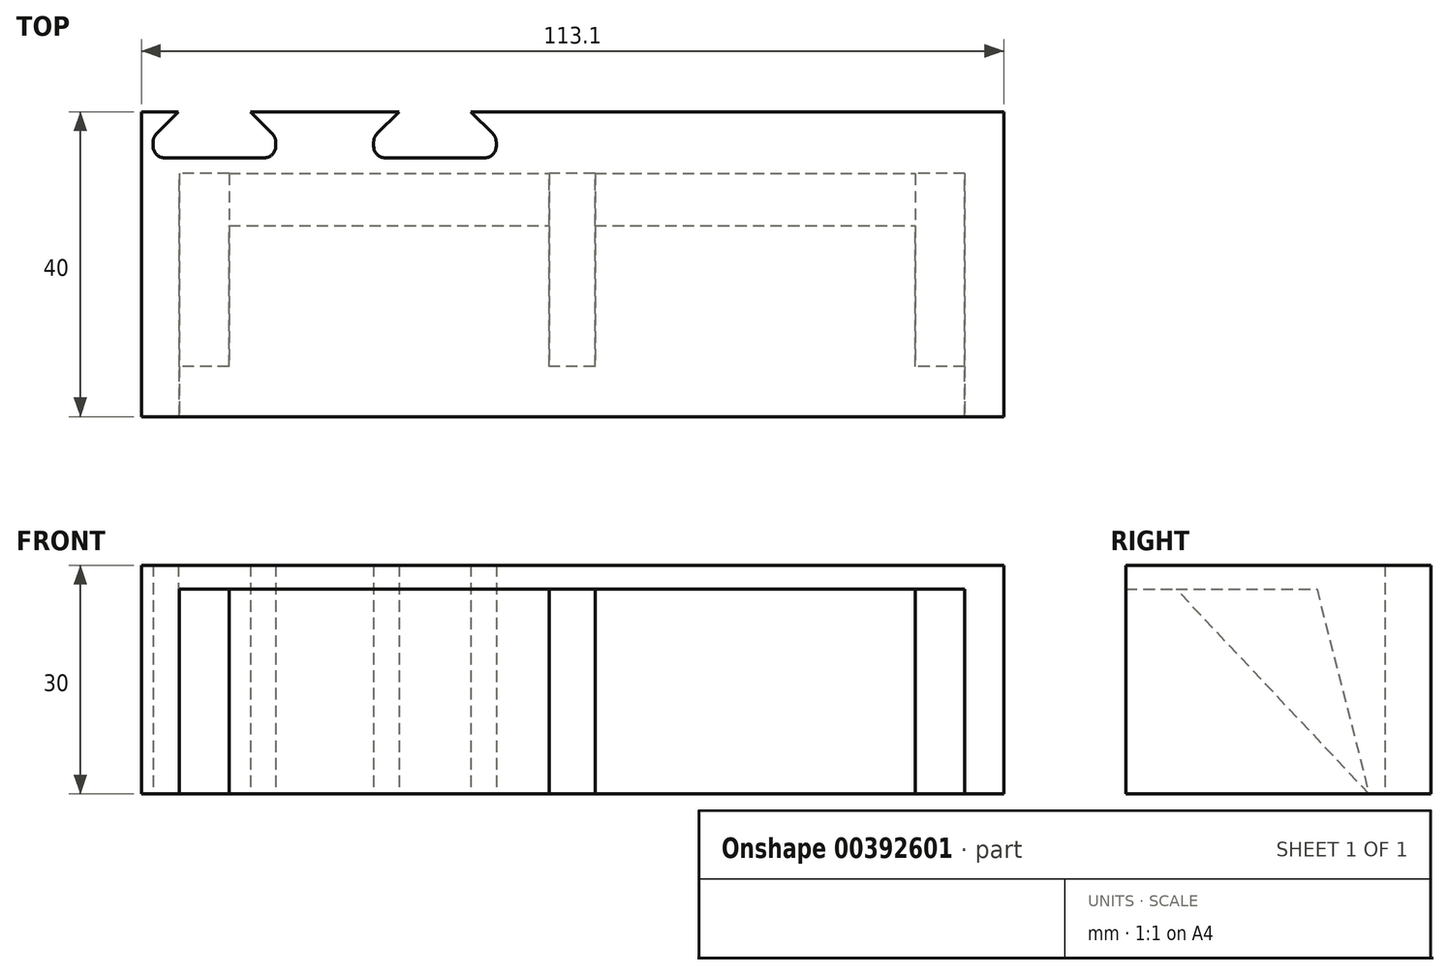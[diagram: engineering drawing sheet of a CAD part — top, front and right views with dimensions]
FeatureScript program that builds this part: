
annotation { "Feature Type Name" : "Feature", "Feature Type Description" : "" }
export const myFeature = defineFeature(function(context is Context, id is Id, definition is map)
    precondition{}
    {
        {
            var Q0;
            Q0=qCreatedBy(makeId("Top.planeOp"),FACE);
            var sketch = newSketch(context, id + "F0", { "sketchPlane" : qUnion([Q0])});
            skLineSegment(sketch, "E0.bottom", {"start": v(90, -35) * mm, "end": v(0, -35) * mm});
            skLineSegment(sketch, "E0.top", {"start": v(90, 35) * mm, "end": v(0, 35) * mm});
            skLineSegment(sketch, "E0.left", {"start": v(90, -35) * mm, "end": v(90, 35) * mm});
            skPoint(sketch, "E0.middle", {"position": v(0, 0) * mm});
            skPoint(sketch, "E1.middle", {"position": v(49.8, 0) * mm});
            skLineSegment(sketch, "E2", {"start": v(0, 0) * mm, "end": v(24, 0) * mm, "construction": true});
            skLineSegment(sketch, "E3", {"start": v(0, 0) * mm, "end": v(0, -14) * mm, "construction": true});
            skLineSegment(sketch, "E4", {"start": v(0, 0) * mm, "end": v(-35, 0) * mm, "construction": true});
            skLineSegment(sketch, "E5.bottom", {"start": v(-5, -19.5) * mm, "end": v(5, -19.5) * mm});
            skLineSegment(sketch, "E5.top", {"start": v(-5, 19.5) * mm, "end": v(5, 19.5) * mm});
            skLineSegment(sketch, "E5.left", {"start": v(-5, -19.5) * mm, "end": v(-5, 19.5) * mm});
            skLineSegment(sketch, "E5.right", {"start": v(5, -19.5) * mm, "end": v(5, 19.5) * mm});
            skLineSegment(sketch, "E6.bottom", {"start": v(-40, -17.25) * mm, "end": v(-30, -17.25) * mm});
            skLineSegment(sketch, "E6.top", {"start": v(-40, 17.25) * mm, "end": v(-30, 17.25) * mm});
            skLineSegment(sketch, "E6.left", {"start": v(-40, -17.25) * mm, "end": v(-40, 17.25) * mm});
            skLineSegment(sketch, "E6.right", {"start": v(-30, -17.25) * mm, "end": v(-30, 17.25) * mm});
            skPoint(sketch, "E6.middle", {"position": v(-35, 0) * mm});
            skLineSegment(sketch, "E7", {"start": v(0, 35) * mm, "end": v(0, 23) * mm});
            skPoint(sketch, "E7.endSnap0", {"position": v(0, 35) * mm});
            skLineSegment(sketch, "E8", {"start": v(0, 23) * mm, "end": v(-50, 23) * mm});
            skLineSegment(sketch, "E9", {"start": v(-50, 23) * mm, "end": v(-50, 0) * mm});
            skLineSegment(sketch, "E10.MirrorCS", {"start": v(-50, -23) * mm, "end": v(-50, 0) * mm});
            skLineSegment(sketch, "E11.MirrorCS", {"start": v(0, -35) * mm, "end": v(0, -23) * mm});
            skLineSegment(sketch, "E12.MirrorCS", {"start": v(0, -23) * mm, "end": v(-50, -23) * mm});
            skPoint(sketch, "E0.right.end.orphan", {"position": v(-90, 35) * mm});
            skPoint(sketch, "E13.orphan", {"position": v(-90, -35) * mm});
            skLineSegment(sketch, "E14.0", {"start": v(92.1, -37.1) * mm, "end": v(92.1, 37.1) * mm});
            skLineSegment(sketch, "E14.1", {"start": v(92.1, -37.1) * mm, "end": v(-2.1, -37.1) * mm});
            skLineSegment(sketch, "E14.2", {"start": v(92.1, 37.1) * mm, "end": v(-2.1, 37.1) * mm});
            skLineSegment(sketch, "E14.3", {"start": v(-2.1, -37.1) * mm, "end": v(-2.1, -25.1) * mm});
            skLineSegment(sketch, "E14.4", {"start": v(-2.1, -25.1) * mm, "end": v(-52.1, -25.1) * mm});
            skLineSegment(sketch, "E14.5", {"start": v(-2.1, 37.1) * mm, "end": v(-2.1, 25.1) * mm});
            skLineSegment(sketch, "E14.6", {"start": v(-2.1, 25.1) * mm, "end": v(-52.1, 25.1) * mm});
            skLineSegment(sketch, "E14.7", {"start": v(-52.1, 25.1) * mm, "end": v(-52.1, 0) * mm});
            skLineSegment(sketch, "E14.8", {"start": v(-52.1, -25.1) * mm, "end": v(-52.1, 0) * mm});
            skLineSegment(sketch, "E15.bottom", {"start": v(-30, 52.75) * mm, "end": v(-40, 52.75) * mm});
            skLineSegment(sketch, "E15.top", {"start": v(-30, 87.25) * mm, "end": v(-40, 87.25) * mm});
            skLineSegment(sketch, "E15.left", {"start": v(-30, 52.75) * mm, "end": v(-30, 87.25) * mm});
            skLineSegment(sketch, "E15.right", {"start": v(-40, 52.75) * mm, "end": v(-40, 87.25) * mm});
            skPoint(sketch, "E15.middle", {"position": v(-35, 70) * mm});
            skLineSegment(sketch, "E16.bottom", {"start": v(-5, 50.5) * mm, "end": v(5, 50.5) * mm});
            skLineSegment(sketch, "E16.top", {"start": v(-5, 89.5) * mm, "end": v(5, 89.5) * mm});
            skLineSegment(sketch, "E16.left", {"start": v(-5, 50.5) * mm, "end": v(-5, 89.5) * mm});
            skLineSegment(sketch, "E16.right", {"start": v(5, 50.5) * mm, "end": v(5, 89.5) * mm});
            skPoint(sketch, "E16.middle", {"position": v(0, 70) * mm});
            skPoint(sketch, "E16.middle.positionSnap0", {"position": v(-30, 70) * mm});
            skPoint(sketch, "E16.centerSnap0", {"position": v(-30, 70) * mm});
            skLineSegment(sketch, "E17", {"start": v(-35, 0) * mm, "end": v(-35, 70) * mm, "construction": true});
            skCircle(sketch, "E18", {"center": v(0, -14) * mm, "radius": 2 * mm});
            skLineSegment(sketch, "E19", {"start": v(-35, 0) * mm, "end": v(-35, -11.75) * mm, "construction": true});
            skCircle(sketch, "E20", {"center": v(-35, -11.75) * mm, "radius": 2 * mm});
            skCircle(sketch, "E21.MirrorC", {"center": v(-35, 11.75) * mm, "radius": 2 * mm});
            skCircle(sketch, "E22.MirrorC", {"center": v(0, 14) * mm, "radius": 2 * mm});
            skLineSegment(sketch, "E23", {"start": v(-35, 70) * mm, "end": v(-35, 81.75) * mm, "construction": true});
            skLineSegment(sketch, "E24", {"start": v(0, 70) * mm, "end": v(0, 84) * mm, "construction": true});
            skCircle(sketch, "E25", {"center": v(-35, 81.75) * mm, "radius": 2 * mm});
            skCircle(sketch, "E26", {"center": v(0, 84) * mm, "radius": 2 * mm});
            skLineSegment(sketch, "E27", {"start": v(-35, 70) * mm, "end": v(-30, 70) * mm, "construction": true});
            skCircle(sketch, "E28.MirrorC", {"center": v(-35, 58.25) * mm, "radius": 2 * mm});
            skCircle(sketch, "E29.MirrorC", {"center": v(0, 56) * mm, "radius": 2 * mm});
            skLineSegment(sketch, "E30", {"start": v(90, -35) * mm, "end": v(92.1, -35) * mm});
            skLineSegment(sketch, "E31", {"start": v(90, 35) * mm, "end": v(92.1, 35) * mm});
            skLineSegment(sketch, "E32", {"start": v(-2.1, 37.1) * mm, "end": v(-6.1, 37.1) * mm});
            skLineSegment(sketch, "E33", {"start": v(-6.1, 37.1) * mm, "end": v(-6.1, 25.1) * mm});
            skLineSegment(sketch, "E34", {"start": v(-2.1, -37.1) * mm, "end": v(-6.1, -37.1) * mm});
            skLineSegment(sketch, "E35", {"start": v(-6.1, -37.1) * mm, "end": v(-6.1, -25.1) * mm});
            skLineSegment(sketch, "E36", {"start": v(-41, 23) * mm, "end": v(-41, 11) * mm});
            skLineSegment(sketch, "E37", {"start": v(-41, 11) * mm, "end": v(-50, 11) * mm});
            skPoint(sketch, "E38.end.orphan", {"position": v(-41, 14.45) * mm});
            skLineSegment(sketch, "E39.MirrorCS", {"start": v(-41, -11) * mm, "end": v(-50, -11) * mm});
            skLineSegment(sketch, "E40.MirrorCS", {"start": v(-41, -23) * mm, "end": v(-41, -11) * mm});
            skLineSegment(sketch, "E41", {"start": v(90, -35) * mm, "end": v(90, -37.1) * mm});
            skLineSegment(sketch, "E42", {"start": v(90, 35) * mm, "end": v(90, 37.1) * mm});
            skLineSegment(sketch, "E43.bottom", {"start": v(90, 35) * mm, "end": v(86, 35) * mm});
            skLineSegment(sketch, "E43.left", {"start": v(90, 35) * mm, "end": v(90, 23) * mm});
            skLineSegment(sketch, "E44.bottom", {"start": v(90, -35) * mm, "end": v(86, -35) * mm});
            skLineSegment(sketch, "E44.left", {"start": v(90, -35) * mm, "end": v(90, -23) * mm});
            skLineSegment(sketch, "E45.bottom", {"start": v(86, -35) * mm, "end": v(80, -35) * mm});
            skLineSegment(sketch, "E46.bottom", {"start": v(86, 35) * mm, "end": v(80, 35) * mm});
            skLineSegment(sketch, "E47.bottom", {"start": v(0, 23) * mm, "end": v(7, 23) * mm});
            skLineSegment(sketch, "E47.top", {"start": v(0, 35) * mm, "end": v(12, 35) * mm});
            skLineSegment(sketch, "E47.left", {"start": v(0, 23) * mm, "end": v(0, 35) * mm});
            skLineSegment(sketch, "E47.right", {"start": v(12, 28) * mm, "end": v(12, 35) * mm});
            skLineSegment(sketch, "E48.bottom", {"start": v(0, -35) * mm, "end": v(12, -35) * mm});
            skLineSegment(sketch, "E48.top", {"start": v(0, -23) * mm, "end": v(7, -23) * mm});
            skLineSegment(sketch, "E48.right", {"start": v(12, -35) * mm, "end": v(12, -28) * mm});
            skCircle(sketch, "E49", {"center": v(6, -29) * mm, "radius": 2 * mm});
            skPoint(sketch, "E49.centerSnap0", {"position": v(6, -35) * mm});
            skPoint(sketch, "E49.centerSnap1", {"position": v(0, -29) * mm});
            skPoint(sketch, "E50.visualSharp", {"position": v(12, -23) * mm});
            skArc(sketch, "E50.filletArc", {"start": v(12, -28) * mm, "mid": v(10.54, -24.46) * mm, "end": v(7, -23) * mm});
            skPoint(sketch, "E51.visualSharp", {"position": v(12, 23) * mm});
            skArc(sketch, "E51.filletArc", {"start": v(7, 23) * mm, "mid": v(10.54, 24.46) * mm, "end": v(12, 28) * mm});
            skCircle(sketch, "E52.MirrorC", {"center": v(6, 29) * mm, "radius": 2 * mm});
            skCircle(sketch, "E53", {"center": v(6, 29) * mm, "radius": 4.5 * mm});
            skCircle(sketch, "E54.MirrorC", {"center": v(6, -29) * mm, "radius": 4.5 * mm});
            skCircle(sketch, "E55", {"center": v(0, 14) * mm, "radius": 6 * mm});
            skCircle(sketch, "E56", {"center": v(-35, 11.75) * mm, "radius": 6 * mm});
            skCircle(sketch, "E57", {"center": v(-35, -11.75) * mm, "radius": 6 * mm});
            skCircle(sketch, "E58", {"center": v(0, -14) * mm, "radius": 6 * mm});
            skLineSegment(sketch, "E59", {"start": v(-6.1, 25.1) * mm, "end": v(-6.08, 23) * mm});
            skLineSegment(sketch, "E60", {"start": v(-6.1, -25.1) * mm, "end": v(-6.1, -23) * mm});
            skLineSegment(sketch, "E61", {"start": v(-47.66, 23) * mm, "end": v(-47.66, 18) * mm, "construction": true});
            skLineSegment(sketch, "E62", {"start": v(-50, 18) * mm, "end": v(-45, 18) * mm, "construction": true});
            skCircle(sketch, "E63", {"center": v(-45, 18) * mm, "radius": 2.25 * mm});
            skCircle(sketch, "E64.MirrorC", {"center": v(-45, -18) * mm, "radius": 2.25 * mm});
            skCircle(sketch, "E65.MirrorC", {"center": v(-25, 18) * mm, "radius": 2.25 * mm});
            skCircle(sketch, "E66.MirrorC", {"center": v(-25, -18) * mm, "radius": 2.25 * mm});
            skCircle(sketch, "E67.MirrorC", {"center": v(28.54, -17.75) * mm, "radius": 2.25 * mm});
            skLineSegment(sketch, "E68.bottom", {"start": v(34.04, -22.75) * mm, "end": v(23.04, -22.75) * mm});
            skLineSegment(sketch, "E68.top", {"start": v(34.04, -12.75) * mm, "end": v(23.04, -12.75) * mm});
            skLineSegment(sketch, "E68.left", {"start": v(36.04, -20.75) * mm, "end": v(36.04, -14.75) * mm});
            skLineSegment(sketch, "E68.right", {"start": v(21.04, -20.75) * mm, "end": v(21.04, -14.75) * mm});
            skLineSegment(sketch, "E69.0", {"start": v(36.44, -12.35) * mm, "end": v(20.64, -12.35) * mm});
            skLineSegment(sketch, "E69.1", {"start": v(36.44, -23.15) * mm, "end": v(36.44, -12.35) * mm});
            skLineSegment(sketch, "E69.2", {"start": v(36.44, -23.15) * mm, "end": v(20.64, -23.15) * mm});
            skLineSegment(sketch, "E69.3", {"start": v(20.64, -23.15) * mm, "end": v(20.64, -12.35) * mm});
            skPoint(sketch, "E70.visualSharp", {"position": v(21.04, -12.75) * mm});
            skArc(sketch, "E70.filletArc", {"start": v(23.04, -12.75) * mm, "mid": v(21.62, -13.33) * mm, "end": v(21.04, -14.75) * mm});
            skPoint(sketch, "E71.visualSharp", {"position": v(36.04, -12.75) * mm});
            skArc(sketch, "E71.filletArc", {"start": v(36.04, -14.75) * mm, "mid": v(35.45, -13.33) * mm, "end": v(34.04, -12.75) * mm});
            skPoint(sketch, "E72.visualSharp", {"position": v(36.04, -22.75) * mm});
            skArc(sketch, "E72.filletArc", {"start": v(34.04, -22.75) * mm, "mid": v(35.45, -22.16) * mm, "end": v(36.04, -20.75) * mm});
            skPoint(sketch, "E73.visualSharp", {"position": v(21.04, -22.75) * mm});
            skArc(sketch, "E73.filletArc", {"start": v(21.04, -20.75) * mm, "mid": v(21.62, -22.16) * mm, "end": v(23.04, -22.75) * mm});
            skArc(sketch, "E74.0", {"start": v(39.54, -14.75) * mm, "mid": v(37.93, -10.86) * mm, "end": v(34.04, -9.25) * mm});
            skLineSegment(sketch, "E74.1", {"start": v(39.54, -20.75) * mm, "end": v(39.54, -14.75) * mm});
            skLineSegment(sketch, "E74.2", {"start": v(34.04, -9.25) * mm, "end": v(23.04, -9.25) * mm});
            skArc(sketch, "E74.3", {"start": v(34.04, -26.25) * mm, "mid": v(37.93, -24.64) * mm, "end": v(39.54, -20.75) * mm});
            skArc(sketch, "E74.4", {"start": v(23.04, -9.25) * mm, "mid": v(19.15, -10.86) * mm, "end": v(17.54, -14.75) * mm});
            skLineSegment(sketch, "E74.5", {"start": v(17.54, -20.75) * mm, "end": v(17.54, -14.75) * mm});
            skArc(sketch, "E74.6", {"start": v(17.54, -20.75) * mm, "mid": v(19.15, -24.64) * mm, "end": v(23.04, -26.25) * mm});
            skLineSegment(sketch, "E74.7", {"start": v(34.04, -26.25) * mm, "end": v(23.04, -26.25) * mm});
            skLineSegment(sketch, "E75", {"start": v(45, 37.1) * mm, "end": v(45, -37.1) * mm});
            skLineSegment(sketch, "E76", {"start": v(45, 31.57) * mm, "end": v(68, 31.57) * mm, "construction": true});
            skLineSegment(sketch, "E77", {"start": v(68, 35) * mm, "end": v(68, -35) * mm});
            skLineSegment(sketch, "E78", {"start": v(12, -28) * mm, "end": v(12, 28) * mm});
            skLineSegment(sketch, "E79", {"start": v(12, 35) * mm, "end": v(12, 37.1) * mm});
            skLineSegment(sketch, "E80", {"start": v(68, 35) * mm, "end": v(68, 37.1) * mm});
            skLineSegment(sketch, "E81", {"start": v(68, 31.57) * mm, "end": v(70.1, 31.57) * mm, "construction": true});
            skLineSegment(sketch, "E82", {"start": v(70.1, 37.1) * mm, "end": v(70.1, -37.1) * mm});
            skLineSegment(sketch, "E83", {"start": v(12, -35) * mm, "end": v(12, -37.1) * mm});
            skLineSegment(sketch, "E84", {"start": v(72.96, 0) * mm, "end": v(72.96, 17.5) * mm, "construction": true});
            skPoint(sketch, "E84.startSnap0", {"position": v(70.1, 0) * mm});
            skLineSegment(sketch, "E85", {"start": v(70.1, 13.5) * mm, "end": v(73.34, 10.26) * mm});
            skPoint(sketch, "E86.end.orphan", {"position": v(71.21, 13.5) * mm});
            skPoint(sketch, "E86.start.orphan", {"position": v(71.21, 17.5) * mm});
            skLineSegment(sketch, "E87", {"start": v(74.05, 9.96) * mm, "end": v(74.64, 9.96) * mm});
            skLineSegment(sketch, "E88", {"start": v(72.96, 17.5) * mm, "end": v(71.21, 17.5) * mm, "construction": true});
            skLineSegment(sketch, "E89.MirrorCS", {"start": v(70.1, 21.5) * mm, "end": v(73.34, 24.74) * mm});
            skLineSegment(sketch, "E90.MirrorCS", {"start": v(74.05, 25.04) * mm, "end": v(74.64, 25.04) * mm});
            skLineSegment(sketch, "E91", {"start": v(75.64, 24.04) * mm, "end": v(75.64, 10.96) * mm});
            skPoint(sketch, "E92.visualSharp", {"position": v(75.64, 25.04) * mm});
            skArc(sketch, "E92.filletArc", {"start": v(75.64, 24.04) * mm, "mid": v(75.34, 24.74) * mm, "end": v(74.64, 25.04) * mm});
            skPoint(sketch, "E93.visualSharp", {"position": v(73.64, 25.04) * mm});
            skArc(sketch, "E93.filletArc", {"start": v(74.05, 25.04) * mm, "mid": v(73.67, 24.96) * mm, "end": v(73.34, 24.74) * mm});
            skPoint(sketch, "E94.visualSharp", {"position": v(73.64, 9.96) * mm});
            skArc(sketch, "E94.filletArc", {"start": v(73.34, 10.26) * mm, "mid": v(73.67, 10.04) * mm, "end": v(74.05, 9.96) * mm});
            skPoint(sketch, "E95.visualSharp", {"position": v(75.64, 9.96) * mm});
            skArc(sketch, "E95.filletArc", {"start": v(74.64, 9.96) * mm, "mid": v(75.34, 10.26) * mm, "end": v(75.64, 10.96) * mm});
            skLineSegment(sketch, "E96.MirrorCS", {"start": v(70.1, -13.5) * mm, "end": v(73.34, -10.26) * mm});
            skArc(sketch, "E97.MirrorCS", {"start": v(73.34, -10.26) * mm, "mid": v(73.67, -10.04) * mm, "end": v(74.05, -9.96) * mm});
            skLineSegment(sketch, "E98.MirrorCS", {"start": v(74.05, -9.96) * mm, "end": v(74.64, -9.96) * mm});
            skArc(sketch, "E99.MirrorCS", {"start": v(74.64, -9.96) * mm, "mid": v(75.34, -10.26) * mm, "end": v(75.64, -10.96) * mm});
            skLineSegment(sketch, "E100.MirrorCS", {"start": v(75.64, -24.04) * mm, "end": v(75.64, -10.96) * mm});
            skLineSegment(sketch, "E101.MirrorCS", {"start": v(70.1, -21.5) * mm, "end": v(73.34, -24.74) * mm});
            skArc(sketch, "E102.MirrorCS", {"start": v(74.05, -25.04) * mm, "mid": v(73.67, -24.96) * mm, "end": v(73.34, -24.74) * mm});
            skLineSegment(sketch, "E103.MirrorCS", {"start": v(74.05, -25.04) * mm, "end": v(74.64, -25.04) * mm});
            skArc(sketch, "E104.MirrorCS", {"start": v(75.64, -24.04) * mm, "mid": v(75.34, -24.74) * mm, "end": v(74.64, -25.04) * mm});
            skLineSegment(sketch, "E105", {"start": v(68, -35) * mm, "end": v(56.64, -23.64) * mm, "construction": true});
            skArc(sketch, "E106.MirrorCS", {"start": v(43.26, -40.34) * mm, "mid": v(43.04, -40.67) * mm, "end": v(42.96, -41.05) * mm});
            skArc(sketch, "E107.MirrorCS", {"start": v(58.04, -41.05) * mm, "mid": v(57.96, -40.67) * mm, "end": v(57.74, -40.34) * mm});
            skArc(sketch, "E108.MirrorCS", {"start": v(42.96, -41.64) * mm, "mid": v(43.26, -42.34) * mm, "end": v(43.96, -42.64) * mm});
            skArc(sketch, "E109.MirrorCS", {"start": v(57.04, -42.64) * mm, "mid": v(57.74, -42.34) * mm, "end": v(58.04, -41.64) * mm});
            skLineSegment(sketch, "E110.MirrorCS", {"start": v(42.96, -41.05) * mm, "end": v(42.96, -41.64) * mm});
            skLineSegment(sketch, "E111.MirrorCS", {"start": v(58.04, -41.05) * mm, "end": v(58.04, -41.64) * mm});
            skLineSegment(sketch, "E112.MirrorCS", {"start": v(57.04, -42.64) * mm, "end": v(43.96, -42.64) * mm});
            skLineSegment(sketch, "E113.MirrorCS", {"start": v(46.5, -37.1) * mm, "end": v(43.26, -40.34) * mm});
            skLineSegment(sketch, "E114.MirrorCS", {"start": v(54.5, -37.1) * mm, "end": v(57.74, -40.34) * mm});
            skLineSegment(sketch, "E115", {"start": v(36.04, -37.1) * mm, "end": v(36.04, -40.15) * mm, "construction": true});
            skLineSegment(sketch, "E116.MirrorCS", {"start": v(14.04, -41.05) * mm, "end": v(14.04, -41.64) * mm});
            skArc(sketch, "E117.MirrorCS", {"start": v(14.04, -41.05) * mm, "mid": v(14.12, -40.67) * mm, "end": v(14.33, -40.34) * mm});
            skLineSegment(sketch, "E118.MirrorCS", {"start": v(29.11, -41.05) * mm, "end": v(29.11, -41.64) * mm});
            skArc(sketch, "E119.MirrorCS", {"start": v(28.82, -40.34) * mm, "mid": v(29.04, -40.67) * mm, "end": v(29.11, -41.05) * mm});
            skArc(sketch, "E120.MirrorCS", {"start": v(15.04, -42.64) * mm, "mid": v(14.33, -42.34) * mm, "end": v(14.04, -41.64) * mm});
            skLineSegment(sketch, "E121.MirrorCS", {"start": v(15.04, -42.64) * mm, "end": v(28.11, -42.64) * mm});
            skArc(sketch, "E122.MirrorCS", {"start": v(29.11, -41.64) * mm, "mid": v(28.82, -42.34) * mm, "end": v(28.11, -42.64) * mm});
            skLineSegment(sketch, "E123.MirrorCS", {"start": v(17.58, -37.1) * mm, "end": v(14.33, -40.34) * mm});
            skLineSegment(sketch, "E124.MirrorCS", {"start": v(25.58, -37.1) * mm, "end": v(28.82, -40.34) * mm});
            skLineSegment(sketch, "E125", {"start": v(28.54, -17.75) * mm, "end": v(28.54, 0) * mm, "construction": true});
            skLineSegment(sketch, "E126", {"start": v(28.54, 0) * mm, "end": v(56.04, 0) * mm, "construction": true});
            skLineSegment(sketch, "E127.bottom", {"start": v(53.54, 20) * mm, "end": v(58.54, 20) * mm});
            skLineSegment(sketch, "E127.top", {"start": v(53.54, -20) * mm, "end": v(58.54, -20) * mm});
            skLineSegment(sketch, "E127.left", {"start": v(53.54, 20) * mm, "end": v(53.54, -20) * mm});
            skLineSegment(sketch, "E127.right", {"start": v(58.54, 20) * mm, "end": v(58.54, -20) * mm});
            skPoint(sketch, "E127.middle", {"position": v(56.04, 0) * mm});
            skLineSegment(sketch, "E128", {"start": v(28.54, -17.75) * mm, "end": v(28.54, -35) * mm, "construction": true});
            skPoint(sketch, "E128.endSnap0", {"position": v(28.54, -26.25) * mm});
            skLineSegment(sketch, "E129", {"start": v(28.54, -17.75) * mm, "end": v(12, -17.75) * mm, "construction": true});
            skLineSegment(sketch, "E130", {"start": v(12, 17.54) * mm, "end": v(28.54, 17.54) * mm, "construction": true});
            skLineSegment(sketch, "E131", {"start": v(28.54, 17.54) * mm, "end": v(28.54, 35) * mm, "construction": true});
            skArc(sketch, "E132.MirrorCS", {"start": v(36.04, 14.75) * mm, "mid": v(35.45, 13.33) * mm, "end": v(34.04, 12.75) * mm});
            skArc(sketch, "E133.MirrorCS", {"start": v(23.04, 12.75) * mm, "mid": v(21.62, 13.33) * mm, "end": v(21.04, 14.75) * mm});
            skArc(sketch, "E134.MirrorCS", {"start": v(21.04, 20.75) * mm, "mid": v(21.62, 22.16) * mm, "end": v(23.04, 22.75) * mm});
            skArc(sketch, "E135.MirrorCS", {"start": v(34.04, 22.75) * mm, "mid": v(35.45, 22.16) * mm, "end": v(36.04, 20.75) * mm});
            skArc(sketch, "E136.MirrorCS", {"start": v(23.04, 9.25) * mm, "mid": v(19.15, 10.86) * mm, "end": v(17.54, 14.75) * mm});
            skLineSegment(sketch, "E137.MirrorCS", {"start": v(34.04, 9.25) * mm, "end": v(23.04, 9.25) * mm});
            skPoint(sketch, "E138.MirrorP", {"position": v(36.04, 12.75) * mm});
            skArc(sketch, "E139.MirrorCS", {"start": v(34.04, 26.25) * mm, "mid": v(37.93, 24.64) * mm, "end": v(39.54, 20.75) * mm});
            skArc(sketch, "E140.MirrorCS", {"start": v(17.54, 20.75) * mm, "mid": v(19.15, 24.64) * mm, "end": v(23.04, 26.25) * mm});
            skPoint(sketch, "E141.MirrorP", {"position": v(28.54, 17.75) * mm});
            skLineSegment(sketch, "E142.MirrorCS", {"start": v(36.44, 23.15) * mm, "end": v(20.64, 23.15) * mm});
            skPoint(sketch, "E143.MirrorP", {"position": v(21.04, 12.75) * mm});
            skLineSegment(sketch, "E144.MirrorCS", {"start": v(34.04, 26.25) * mm, "end": v(23.04, 26.25) * mm});
            skPoint(sketch, "E145.MirrorP", {"position": v(21.04, 22.75) * mm});
            skLineSegment(sketch, "E146.MirrorCS", {"start": v(20.64, 23.15) * mm, "end": v(20.64, 12.35) * mm});
            skLineSegment(sketch, "E147.MirrorCS", {"start": v(36.44, 12.35) * mm, "end": v(20.64, 12.35) * mm});
            skLineSegment(sketch, "E148.MirrorCS", {"start": v(17.54, 20.75) * mm, "end": v(17.54, 14.75) * mm});
            skCircle(sketch, "E149.MirrorC", {"center": v(28.54, 17.75) * mm, "radius": 2.25 * mm});
            skPoint(sketch, "E150.MirrorP", {"position": v(28.54, 26.25) * mm});
            skPoint(sketch, "E151.MirrorP", {"position": v(36.04, 22.75) * mm});
            skLineSegment(sketch, "E152.MirrorCS", {"start": v(21.04, 20.75) * mm, "end": v(21.04, 14.75) * mm});
            skLineSegment(sketch, "E153.MirrorCS", {"start": v(39.54, 20.75) * mm, "end": v(39.54, 14.75) * mm});
            skLineSegment(sketch, "E154.MirrorCS", {"start": v(36.44, 23.15) * mm, "end": v(36.44, 12.35) * mm});
            skLineSegment(sketch, "E155.MirrorCS", {"start": v(34.04, 22.75) * mm, "end": v(23.04, 22.75) * mm});
            skArc(sketch, "E156.MirrorCS", {"start": v(39.54, 14.75) * mm, "mid": v(37.93, 10.86) * mm, "end": v(34.04, 9.25) * mm});
            skLineSegment(sketch, "E157.MirrorCS", {"start": v(34.04, 12.75) * mm, "end": v(23.04, 12.75) * mm});
            skLineSegment(sketch, "E158.MirrorCS", {"start": v(36.04, 20.75) * mm, "end": v(36.04, 14.75) * mm});
            skArc(sketch, "E159.MirrorCS", {"start": v(29.11, 41.64) * mm, "mid": v(28.82, 42.34) * mm, "end": v(28.11, 42.64) * mm});
            skArc(sketch, "E160.MirrorCS", {"start": v(28.82, 40.34) * mm, "mid": v(29.04, 40.67) * mm, "end": v(29.11, 41.05) * mm});
            skArc(sketch, "E161.MirrorCS", {"start": v(15.04, 42.64) * mm, "mid": v(14.33, 42.34) * mm, "end": v(14.04, 41.64) * mm});
            skArc(sketch, "E162.MirrorCS", {"start": v(14.04, 41.05) * mm, "mid": v(14.12, 40.67) * mm, "end": v(14.33, 40.34) * mm});
            skArc(sketch, "E163.MirrorCS", {"start": v(57.04, 42.64) * mm, "mid": v(57.74, 42.34) * mm, "end": v(58.04, 41.64) * mm});
            skArc(sketch, "E164.MirrorCS", {"start": v(58.04, 41.05) * mm, "mid": v(57.96, 40.67) * mm, "end": v(57.74, 40.34) * mm});
            skLineSegment(sketch, "E165.MirrorCS", {"start": v(42.96, 41.05) * mm, "end": v(42.96, 41.64) * mm});
            skLineSegment(sketch, "E166.MirrorCS", {"start": v(58.04, 41.05) * mm, "end": v(58.04, 41.64) * mm});
            skLineSegment(sketch, "E167.MirrorCS", {"start": v(14.04, 41.05) * mm, "end": v(14.04, 41.64) * mm});
            skLineSegment(sketch, "E168.MirrorCS", {"start": v(29.11, 41.05) * mm, "end": v(29.11, 41.64) * mm});
            skArc(sketch, "E169.MirrorCS", {"start": v(42.96, 41.64) * mm, "mid": v(43.26, 42.34) * mm, "end": v(43.96, 42.64) * mm});
            skArc(sketch, "E170.MirrorCS", {"start": v(43.26, 40.34) * mm, "mid": v(43.04, 40.67) * mm, "end": v(42.96, 41.05) * mm});
            skLineSegment(sketch, "E171.MirrorCS", {"start": v(57.04, 42.64) * mm, "end": v(43.96, 42.64) * mm});
            skLineSegment(sketch, "E172.MirrorCS", {"start": v(15.04, 42.64) * mm, "end": v(28.11, 42.64) * mm});
            skLineSegment(sketch, "E173.MirrorCS", {"start": v(17.58, 37.1) * mm, "end": v(14.33, 40.34) * mm});
            skLineSegment(sketch, "E174.MirrorCS", {"start": v(25.58, 37.1) * mm, "end": v(28.82, 40.34) * mm});
            skLineSegment(sketch, "E175.MirrorCS", {"start": v(46.5, 37.1) * mm, "end": v(43.26, 40.34) * mm});
            skLineSegment(sketch, "E176.MirrorCS", {"start": v(54.5, 37.1) * mm, "end": v(57.74, 40.34) * mm});
            skLineSegment(sketch, "E177", {"start": v(92.1, 37.1) * mm, "end": v(125.1, 37.1) * mm});
            skLineSegment(sketch, "E178", {"start": v(125.1, 37.1) * mm, "end": v(125.1, -37.1) * mm});
            skLineSegment(sketch, "E179", {"start": v(125.1, -37.1) * mm, "end": v(92.1, -37.1) * mm});
            skLineSegment(sketch, "E180", {"start": v(125.1, 30.14) * mm, "end": v(123, 30.14) * mm, "construction": true});
            skLineSegment(sketch, "E181.0", {"start": v(70.1, 12.8) * mm, "end": v(72.99, 9.9) * mm});
            skArc(sketch, "E181.1", {"start": v(72.99, 9.9) * mm, "mid": v(73.48, 9.58) * mm, "end": v(74.05, 9.46) * mm});
            skLineSegment(sketch, "E181.2", {"start": v(74.05, 9.46) * mm, "end": v(74.64, 9.46) * mm});
            skArc(sketch, "E181.3", {"start": v(74.64, 9.46) * mm, "mid": v(75.7, 9.9) * mm, "end": v(76.14, 10.96) * mm});
            skLineSegment(sketch, "E181.4", {"start": v(76.14, 24.04) * mm, "end": v(76.14, 10.96) * mm});
            skLineSegment(sketch, "E181.5", {"start": v(70.1, 22.2) * mm, "end": v(72.99, 25.1) * mm});
            skArc(sketch, "E181.6", {"start": v(74.05, 25.54) * mm, "mid": v(73.48, 25.42) * mm, "end": v(72.99, 25.1) * mm});
            skLineSegment(sketch, "E181.7", {"start": v(74.05, 25.54) * mm, "end": v(74.64, 25.54) * mm});
            skArc(sketch, "E181.8", {"start": v(76.14, 24.04) * mm, "mid": v(75.7, 25.1) * mm, "end": v(74.64, 25.54) * mm});
            skLineSegment(sketch, "E182.MirrorCS", {"start": v(70.1, -12.8) * mm, "end": v(72.99, -9.9) * mm});
            skArc(sketch, "E183.MirrorCS", {"start": v(72.99, -9.9) * mm, "mid": v(73.48, -9.58) * mm, "end": v(74.05, -9.46) * mm});
            skLineSegment(sketch, "E184.MirrorCS", {"start": v(74.05, -9.46) * mm, "end": v(74.64, -9.46) * mm});
            skArc(sketch, "E185.MirrorCS", {"start": v(74.64, -9.46) * mm, "mid": v(75.7, -9.9) * mm, "end": v(76.14, -10.96) * mm});
            skLineSegment(sketch, "E186.MirrorCS", {"start": v(76.14, -24.04) * mm, "end": v(76.14, -10.96) * mm});
            skArc(sketch, "E187.MirrorCS", {"start": v(76.14, -24.04) * mm, "mid": v(75.7, -25.1) * mm, "end": v(74.64, -25.54) * mm});
            skLineSegment(sketch, "E188.MirrorCS", {"start": v(74.05, -25.54) * mm, "end": v(74.64, -25.54) * mm});
            skArc(sketch, "E189.MirrorCS", {"start": v(74.05, -25.54) * mm, "mid": v(73.48, -25.42) * mm, "end": v(72.99, -25.1) * mm});
            skLineSegment(sketch, "E190.MirrorCS", {"start": v(70.1, -22.2) * mm, "end": v(72.99, -25.1) * mm});
            skLineSegment(sketch, "E191.0", {"start": v(45.8, -37.1) * mm, "end": v(42.9, -39.99) * mm});
            skArc(sketch, "E191.1", {"start": v(42.9, -39.99) * mm, "mid": v(42.58, -40.48) * mm, "end": v(42.46, -41.05) * mm});
            skLineSegment(sketch, "E191.2", {"start": v(42.46, -41.05) * mm, "end": v(42.46, -41.64) * mm});
            skArc(sketch, "E191.3", {"start": v(42.46, -41.64) * mm, "mid": v(42.9, -42.7) * mm, "end": v(43.96, -43.14) * mm});
            skLineSegment(sketch, "E191.4", {"start": v(57.04, -43.14) * mm, "end": v(43.96, -43.14) * mm});
            skLineSegment(sketch, "E191.5", {"start": v(55.2, -37.1) * mm, "end": v(58.1, -39.99) * mm});
            skArc(sketch, "E191.6", {"start": v(58.54, -41.05) * mm, "mid": v(58.42, -40.48) * mm, "end": v(58.1, -39.99) * mm});
            skLineSegment(sketch, "E191.7", {"start": v(58.54, -41.05) * mm, "end": v(58.54, -41.64) * mm});
            skArc(sketch, "E191.8", {"start": v(57.04, -43.14) * mm, "mid": v(58.1, -42.7) * mm, "end": v(58.54, -41.64) * mm});
            skLineSegment(sketch, "E192.MirrorCS", {"start": v(26.28, -37.1) * mm, "end": v(29.17, -39.99) * mm});
            skArc(sketch, "E193.MirrorCS", {"start": v(29.17, -39.99) * mm, "mid": v(29.5, -40.48) * mm, "end": v(29.61, -41.05) * mm});
            skLineSegment(sketch, "E194.MirrorCS", {"start": v(29.61, -41.05) * mm, "end": v(29.61, -41.64) * mm});
            skArc(sketch, "E195.MirrorCS", {"start": v(29.61, -41.64) * mm, "mid": v(29.17, -42.7) * mm, "end": v(28.11, -43.14) * mm});
            skLineSegment(sketch, "E196.MirrorCS", {"start": v(15.04, -43.14) * mm, "end": v(28.11, -43.14) * mm});
            skArc(sketch, "E197.MirrorCS", {"start": v(15.04, -43.14) * mm, "mid": v(13.98, -42.7) * mm, "end": v(13.54, -41.64) * mm});
            skLineSegment(sketch, "E198.MirrorCS", {"start": v(13.54, -41.05) * mm, "end": v(13.54, -41.64) * mm});
            skArc(sketch, "E199.MirrorCS", {"start": v(13.54, -41.05) * mm, "mid": v(13.66, -40.48) * mm, "end": v(13.98, -39.99) * mm});
            skLineSegment(sketch, "E200.MirrorCS", {"start": v(16.87, -37.1) * mm, "end": v(13.98, -39.99) * mm});
            skLineSegment(sketch, "E201", {"start": v(12, -37.1) * mm, "end": v(12, -77.1) * mm});
            skLineSegment(sketch, "E202", {"start": v(12, -77.1) * mm, "end": v(125.1, -77.1) * mm});
            skLineSegment(sketch, "E203", {"start": v(125.1, -77.1) * mm, "end": v(125.1, -37.1) * mm});
            skSolve(sketch);
        }
        {
            var Q0;
            {var subQ9=sQuery(id+"F0.wireOp",EDGE,"E179");Q0=makeQuery(id+"F0.imprint","IMPRINT",FACE,{"disambiguationData":[TD([[makeQuery(id+"F0.imprint","IMPRINT",EDGE,{"derivedFrom":subQ9}),1.0]])]});}
            extrude(context, id + "F1", {"entities" : qUnion([Q0]), "depth" : 30 * mm});
        }
        {
            var Q0;
            Q0=qCreatedBy(makeId("Right.planeOp"),FACE);
            cPlane(context, id + "F2", {"entities" : qUnion([Q0]), "cplaneType" : CPlaneType.OFFSET, "offset" : 68.5 * mm, "width" : 150 * mm, "height" : 150 * mm});
        }
        {
            var Q0;
            Q0=qCreatedBy(id+"F2.planeOp",FACE);
            var sketch = newSketch(context, id + "F3", { "sketchPlane" : qUnion([Q0])});
            skLineSegment(sketch, "E204", {"start": v(0, 0) * mm, "end": v(-77.2, 0) * mm});
            skLineSegment(sketch, "E205", {"start": v(-77.2, 0) * mm, "end": v(-77.2, 26.9) * mm});
            skLineSegment(sketch, "E206", {"start": v(-77.2, 26.9) * mm, "end": v(-45.2, 26.9) * mm});
            skLineSegment(sketch, "E207", {"start": v(-45.2, 26.9) * mm, "end": v(-45.2, 0) * mm});
            skLineSegment(sketch, "E208", {"start": v(-45.2, 0) * mm, "end": v(-70.5, 26.9) * mm});
            skLineSegment(sketch, "E209", {"start": v(-45.2, 0) * mm, "end": v(-52.03, 26.9) * mm});
            skSolve(sketch);
        }
        {
            var Q0;
            Q0 = qSketchRegion(id + "F3", true);
            extrude(context, id + "F4", {"entities" : qUnion([Q0]), "operationType" : NewBodyOperationType.REMOVE, "endBound" : BoundingType.SYMMETRIC, "depth" : 103 * mm});
        }
        {
            var Q0;
            {var subQ0=sQuery(id+"F3.wireOp",EDGE,"E207");Q0=makeQuery(id+"F3.imprint","IMPRINT",FACE,{"disambiguationData":[TD([[makeQuery(id+"F3.imprint","IMPRINT",EDGE,{"derivedFrom":subQ0}),-1.0]])]});}
            var Q1;
            {var subQ0=sQuery(id+"F3.wireOp",EDGE,"E208");Q1=makeQuery(id+"F3.imprint","IMPRINT",FACE,{"disambiguationData":[TD([[makeQuery(id+"F3.imprint","IMPRINT",EDGE,{"derivedFrom":subQ0}),-1.0]])]});}
            extrude(context, id + "F5", {"entities" : qUnion([Q0, Q1]), "operationType" : NewBodyOperationType.ADD, "endBound" : BoundingType.SYMMETRIC, "depth" : 107 * mm});
        }
        {
            var Q0;
            {var subQ0=sQuery(id+"F3.wireOp",EDGE,"E208");Q0=makeQuery(id+"F3.imprint","IMPRINT",FACE,{"disambiguationData":[TD([[makeQuery(id+"F3.imprint","IMPRINT",EDGE,{"derivedFrom":subQ0}),-1.0]])]});}
            extrude(context, id + "F6", {"entities" : qUnion([Q0]), "operationType" : NewBodyOperationType.REMOVE, "endBound" : BoundingType.SYMMETRIC, "oppositeDirection" : true, "depth" : 90 * mm});
        }
        {
            var Q0;
            {var subQ0=sQuery(id+"F3.wireOp",EDGE,"E207");Q0=makeQuery(id+"F3.imprint","IMPRINT",FACE,{"disambiguationData":[TD([[makeQuery(id+"F3.imprint","IMPRINT",EDGE,{"derivedFrom":subQ0}),-1.0]])]});}
            var Q1;
            {var subQ0=sQuery(id+"F3.wireOp",EDGE,"E208");Q1=makeQuery(id+"F3.imprint","IMPRINT",FACE,{"disambiguationData":[TD([[makeQuery(id+"F3.imprint","IMPRINT",EDGE,{"derivedFrom":subQ0}),-1.0]])]});}
            extrude(context, id + "F7", {"entities" : qUnion([Q0, Q1]), "operationType" : NewBodyOperationType.ADD, "endBound" : BoundingType.SYMMETRIC, "depth" : 6 * mm});
        }
    });
